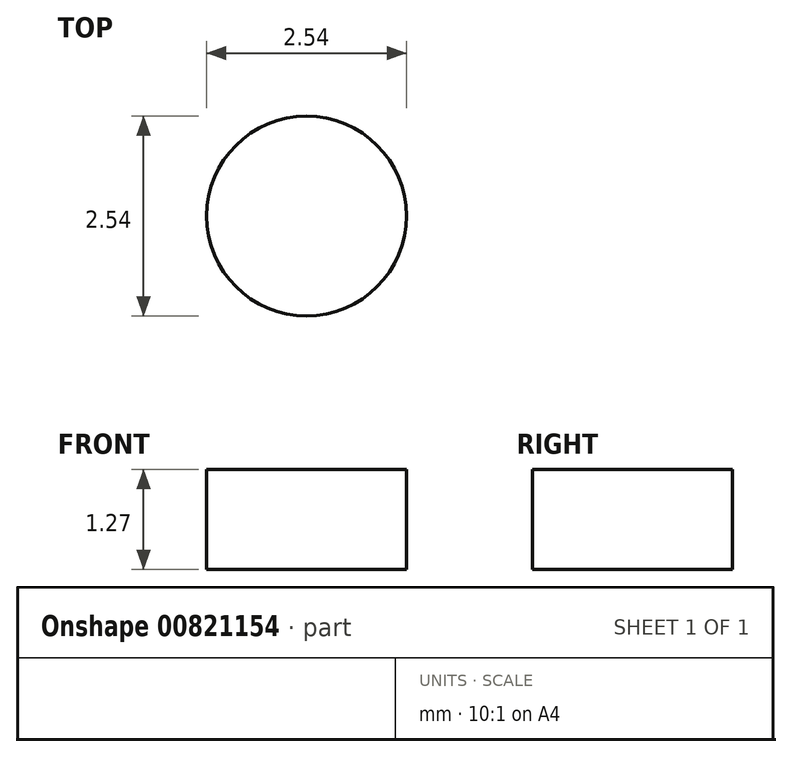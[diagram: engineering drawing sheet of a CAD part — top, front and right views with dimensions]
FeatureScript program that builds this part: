
annotation { "Feature Type Name" : "Feature", "Feature Type Description" : "" }
export const myFeature = defineFeature(function(context is Context, id is Id, definition is map)
    precondition{}
    {
        {
            var Q0;
            Q0=qCreatedBy(makeId("Top.planeOp"),FACE);
            var sketch = newSketch(context, id + "F0", { "sketchPlane" : qUnion([Q0])});
            skCircle(sketch, "E0", {"center": v(0, 0) * mm, "radius": 1.27 * mm});
            skSolve(sketch);
        }
        {
            var Q0;
            Q0 = qSketchRegion(id + "F0", true);
            var Q1;
            Q1=makeQuery(id+"F0.imprint","IMPRINT",FACE,{"disambiguationData":[TD([[makeQuery(id+"F0.imprint","IMPRINT",EDGE,{"derivedFrom":sQuery(id+"F0.wireOp",EDGE,"E0")}),1.0]])]});
            extrude(context, id + "F1", {"entities" : qUnion([Q0, Q1]), "depth" : 1.27 * mm, "offsetDistance" : 25.4 * mm});
        }
    });
